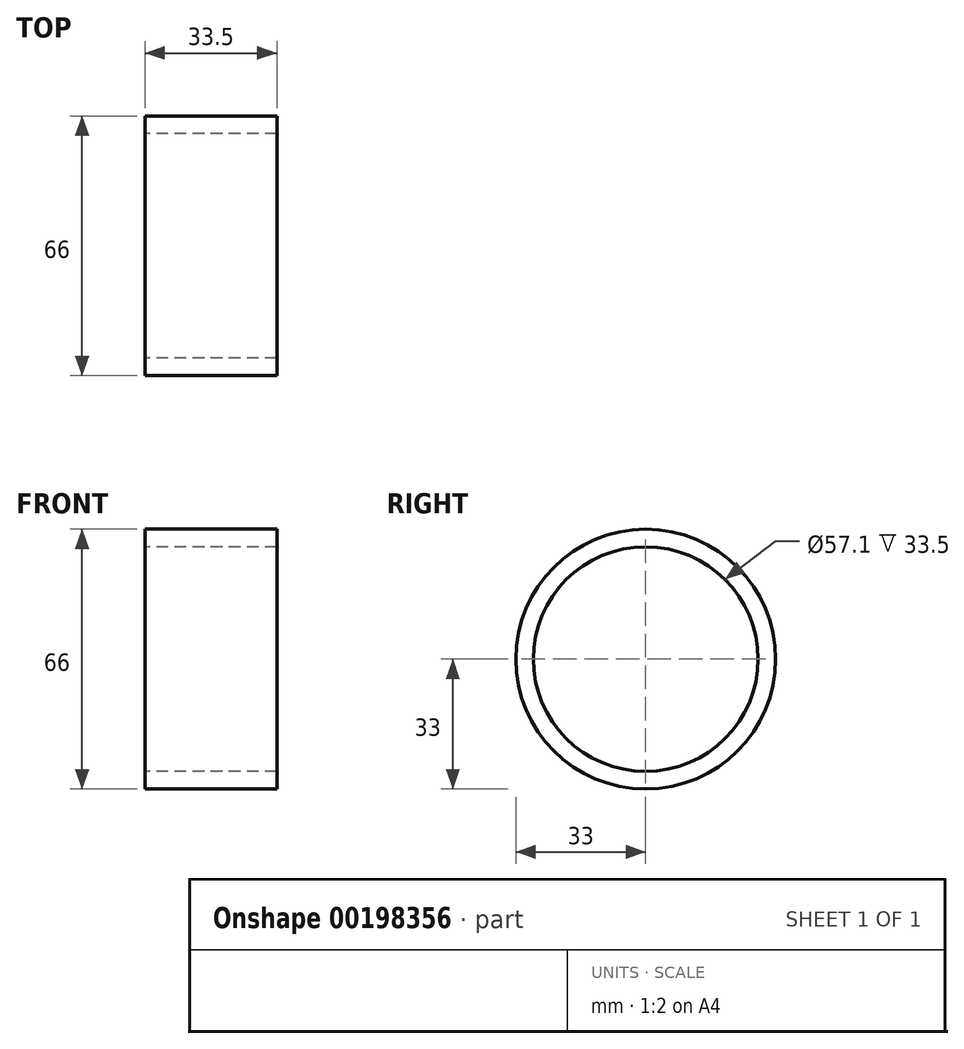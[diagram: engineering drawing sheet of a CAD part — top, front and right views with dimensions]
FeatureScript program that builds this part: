
annotation { "Feature Type Name" : "Feature", "Feature Type Description" : "" }
export const myFeature = defineFeature(function(context is Context, id is Id, definition is map)
    precondition{}
    {
        {
            var Q0;
            Q0=qCreatedBy(makeId("Right.planeOp"),FACE);
            var sketch = newSketch(context, id + "F0", { "sketchPlane" : qUnion([Q0])});
            skCircle(sketch, "E0", {"center": v(0, 0) * mm, "radius": 28.55 * mm});
            skCircle(sketch, "E1", {"center": v(0, 0) * mm, "radius": 33 * mm});
            skSolve(sketch);
        }
        {
            var Q0;
            Q0=qSketchRegion(id+"F0",true);
            extrude(context, id + "F1", {"entities" : qUnion([Q0]), "depth" : (25 + 8.5) * mm});
        }
    });
